FCSTD DOCUMENT  (FreeCAD 0.19R24291 (Git))
Label: Probem 08.pdf
License: All rights reserved
LicenseURL: http://en.wikipedia.org/wiki/All_rights_reserved
objects: Part::Part2DObjectPython×36, App::FeaturePython×35
note: 36 computed .brp shape members not serialized (recipe doc carries the construction recipe); baked Part::Feature solids carry a one-line shape summary decoded from their .brp

FEATURE [Part::Part2DObjectPython] Polygon  # Draft 2D object (typed FeaturePython)
  Area = 0
  ChamferSize = 0
  DrawMode = 0
  FacesNumber = 6
  FilletRadius = 0
  MakeFace = false
  Placement = pos=(-17.9158,-59.1281,0) rot=(0,0,-1;1.5708rad)
  Radius = 25
FEATURE [App::FeaturePython] Text  # WARN: FeaturePython — macro-defined, semantics opaque (R4)
  Placement = pos=(-43.3968,-74.2912,0) rot=(0,0,1;0rad)
  Text = a
FEATURE [App::FeaturePython] Text001  # WARN: FeaturePython — macro-defined, semantics opaque (R4)
  Placement = pos=(-18.9407,-88.9649,0) rot=(0,0,1;0rad)
  Text = b
FEATURE [App::FeaturePython] Text002  # WARN: FeaturePython — macro-defined, semantics opaque (R4)
  Placement = pos=(4.49643,-75.514,0) rot=(0,0,1;0rad)
  Text = c
FEATURE [App::FeaturePython] Text003  # WARN: FeaturePython — macro-defined, semantics opaque (R4)
  Placement = pos=(4.29263,-45.759,0) rot=(0,0,1;0rad)
  Text = d
FEATURE [App::FeaturePython] Text004  # WARN: FeaturePython — macro-defined, semantics opaque (R4)
  Placement = pos=(-16.9027,-31.9005,0) rot=(0,0,1;0rad)
  Text = e
FEATURE [App::FeaturePython] Text005  # WARN: FeaturePython — macro-defined, semantics opaque (R4)
  Placement = pos=(-43.3968,-44.1286,0) rot=(0,0,1;0rad)
  Text = f
FEATURE [App::FeaturePython] Text006  # WARN: FeaturePython — macro-defined, semantics opaque (R4)
  Placement = pos=(-17.9158,-59.1281,0) rot=(0,0,1;0rad)
  Text = O
FEATURE [Part::Part2DObjectPython] Line  # Draft 2D object (typed FeaturePython)
  Area = 0
  ChamferSize = 0
  Closed = false
  End = (-39.5664,-8.08368,0)
  FilletRadius = 0
  Length = 38.5445
  MakeFace = false
  Placement = pos=(-39.5664,-46.6281,0) rot=(0,0,1;0rad)
  Points = (2) [(0,0,0),(0,38.5445,0)]
  Start = (-39.5664,-46.6281,0)
  Subdivisions = 0
FEATURE [Part::Part2DObjectPython] Line002  # Draft 2D object (typed FeaturePython)
  Area = 0
  ChamferSize = 0
  Closed = false
  End = (-17.9158,-8.08368,0)
  FilletRadius = 0
  Length = 26.0445
  MakeFace = false
  Placement = pos=(-17.9158,-34.1281,0) rot=(0,0,1;0rad)
  Points = (2) [(0,0,0),(7.10543e-15,26.0445,0)]
  Start = (-17.9158,-34.1281,0)
  Subdivisions = 0
FEATURE [Part::Part2DObjectPython] Line003  # Draft 2D object (typed FeaturePython)
  Area = 0
  ChamferSize = 0
  Closed = false
  End = (3.73485,-8.08368,0)
  FilletRadius = 0
  Length = 38.5445
  MakeFace = false
  Placement = pos=(3.73485,-46.6281,0) rot=(0,0,1;0rad)
  Points = (2) [(0,0,0),(1.73195e-14,38.5445,0)]
  Start = (3.73485,-46.6281,0)
  Subdivisions = 0
FEATURE [Part::Part2DObjectPython] Line005  # Draft 2D object (typed FeaturePython)
  Area = 0
  ChamferSize = 0
  Closed = false
  End = (-29.4668,15.2405,0)
  FilletRadius = 0
  Length = 25.4169
  MakeFace = false
  Placement = pos=(-39.5664,-8.08368,0) rot=(0,0,1;0rad)
  Points = (2) [(0,0,0),(10.0997,23.3242,0)]
  Start = (-39.5664,-8.08368,0)
  Subdivisions = 0
FEATURE [Part::Part2DObjectPython] Line007  # Draft 2D object (typed FeaturePython)
  Area = 0
  ChamferSize = 0
  Closed = false
  End = (3.73485,-46.6281,0)
  FilletRadius = 0
  Length = 50
  MakeFace = false
  Placement = pos=(-39.5664,-71.6281,0) rot=(0,0,1;0rad)
  Points = (2) [(0,0,0),(43.3013,25,0)]
  Start = (-39.5664,-71.6281,0)
  Subdivisions = 0
FEATURE [Part::Part2DObjectPython] Line008  # Draft 2D object (typed FeaturePython)
  Area = 0
  ChamferSize = 0
  Closed = false
  End = (-39.5664,-46.6281,0)
  FilletRadius = 0
  Length = 50
  MakeFace = false
  Placement = pos=(3.73485,-71.6281,0) rot=(0,0,1;0rad)
  Points = (2) [(0,0,0),(-43.3013,25,0)]
  Start = (3.73485,-71.6281,0)
  Subdivisions = 0
FEATURE [Part::Part2DObjectPython] Line009  # Draft 2D object (typed FeaturePython)
  Area = 0
  ChamferSize = 0
  Closed = false
  End = (-17.9158,-34.1281,0)
  FilletRadius = 0
  Length = 50
  MakeFace = false
  Placement = pos=(-17.9158,-84.1281,0) rot=(0,0,1;0rad)
  Points = (2) [(0,0,0),(2.84217e-14,50,0)]
  Start = (-17.9158,-84.1281,0)
  Subdivisions = 0
FEATURE [Part::Part2DObjectPython] Line010  # Draft 2D object (typed FeaturePython)
  Area = 0
  ChamferSize = 0
  Closed = false
  End = (-17.9158,21.9163,0)
  FilletRadius = 0
  Length = 20
  MakeFace = false
  Placement = pos=(-17.9158,41.9163,0) rot=(0,0,1;0rad)
  Points = (2) [(0,0,0),(0,-20,0)]
  Start = (-17.9158,41.9163,0)
  Subdivisions = 0
FEATURE [Part::Part2DObjectPython] Line012  # Draft 2D object (typed FeaturePython)
  Area = 0
  ChamferSize = 0
  Closed = false
  End = (-69.8239,-8.08368,0)
  FilletRadius = 0
  Length = 88.0582
  MakeFace = false
  Placement = pos=(-17.9158,21.9163,0) rot=(0,0,1;0rad)
  Points = (2) [(24.333,14.0631,0),(-51.9081,-30,0)]
  Start = (6.41717,35.9794,0)
  Subdivisions = 0
FEATURE [App::FeaturePython] Text008  # WARN: FeaturePython — macro-defined, semantics opaque (R4)
  Placement = pos=(-42.9752,-12.9467,0) rot=(0,0,1;0rad)
  Text = a'(f')
FEATURE [App::FeaturePython] Text009  # WARN: FeaturePython — macro-defined, semantics opaque (R4)
  Placement = pos=(-21.1684,-12.9467,0) rot=(0,0,1;0rad)
  Text = b'(e')
FEATURE [App::FeaturePython] Text010  # WARN: FeaturePython — macro-defined, semantics opaque (R4)
  Placement = pos=(-2.82633,-12.9467,0) rot=(0,0,1;0rad)
  Text = c'(d')
FEATURE [App::FeaturePython] Text011  # WARN: FeaturePython — macro-defined, semantics opaque (R4)
  Placement = pos=(-79.6594,-5.81369,0) rot=(0,0,1;0rad)
  Text = VP
FEATURE [App::FeaturePython] Text012  # WARN: FeaturePython — macro-defined, semantics opaque (R4)
  Placement = pos=(-79.4556,-14.5771,0) rot=(0,0,1;0rad)
  Text = HP
FEATURE [App::FeaturePython] Text013  # WARN: FeaturePython — macro-defined, semantics opaque (R4)
  Placement = pos=(-41.5486,16.1968,0) rot=(0,0,1;0rad)
  Text = 1'(6')
FEATURE [App::FeaturePython] Text014  # WARN: FeaturePython — macro-defined, semantics opaque (R4)
  Placement = pos=(-25.6521,21.6995,0) rot=(0,0,1;0rad)
  Text = 2'(5')
FEATURE [App::FeaturePython] Text015  # WARN: FeaturePython — macro-defined, semantics opaque (R4)
  Placement = pos=(-12.7219,28.1305,0) rot=(0,0,1;0rad)
  Text = 3'(4')
FEATURE [Part::Part2DObjectPython] Line015  # Draft 2D object (typed FeaturePython)
  Area = 0
  ChamferSize = 0
  Closed = false
  End = (-17.9158,21.9163,0)
  FilletRadius = 0
  Length = 30
  MakeFace = false
  Placement = pos=(-17.9158,-8.08368,0) rot=(0,0,1;0rad)
  Points = (2) [(0,0,0),(0,30,0)]
  Start = (-17.9158,-8.08368,0)
  Subdivisions = 0
FEATURE [Part::Part2DObjectPython] Arc  # Draft 2D object (typed FeaturePython)
  Area = 0
  FirstAngle = -30
  LastAngle = 0
  MakeFace = false
  Placement = pos=(-17.9158,-59.1281,0) rot=(0,0,1;0rad)
  Radius = 25
FEATURE [Part::Part2DObjectPython] Line017  # Draft 2D object (typed FeaturePython)
  Area = 0
  ChamferSize = 0
  Closed = false
  End = (7.08421,-8.08368,0)
  FilletRadius = 0
  Length = 51.0445
  MakeFace = false
  Placement = pos=(7.08421,-59.1281,0) rot=(0,0,1;0rad)
  Points = (2) [(0,0,0),(-1.77636e-15,51.0445,0)]
  Start = (7.08421,-59.1281,0)
  Subdivisions = 0
FEATURE [Part::Part2DObjectPython] Line018  # Draft 2D object (typed FeaturePython)
  Area = 0
  ChamferSize = 0
  Closed = false
  End = (-10.989,25.9196,0)
  FilletRadius = 0
  Length = 38.508
  MakeFace = false
  Placement = pos=(7.08421,-8.08368,0) rot=(0,0,1;0rad)
  Points = (2) [(0,0,0),(-18.0732,34.0033,0)]
  Start = (7.08421,-8.08368,0)
  Subdivisions = 0
FEATURE [Part::Part2DObjectPython] Line019  # Draft 2D object (typed FeaturePython)
  Area = 0
  ChamferSize = 0
  Closed = false
  End = (-17.9158,41.9163,0)
  FilletRadius = 0
  Length = 29.0693
  MakeFace = false
  Placement = pos=(-39.5664,-8.08368,0) rot=(0,0,1;0rad)
  Points = (2) [(10.0997,23.3242,0),(21.6506,50,0)]
  Start = (-29.4668,15.2405,0)
  Subdivisions = 0
FEATURE [Part::Part2DObjectPython] Line020  # Draft 2D object (typed FeaturePython)
  Area = 0
  ChamferSize = 0
  Closed = false
  End = (-9.25553,21.9163,0)
  FilletRadius = 0
  Length = 0
  MakeFace = false
  Placement = pos=(-9.25553,21.9163,0) rot=(0,0,1;0rad)
  Points = (2) [(0,0,0),(0,3.55271e-15,0)]
  Start = (-9.25553,21.9163,0)
  Subdivisions = 0
FEATURE [Part::Part2DObjectPython] Line021  # Draft 2D object (typed FeaturePython)
  Area = 0
  ChamferSize = 0
  Closed = false
  End = (-9.25553,21.9163,0)
  FilletRadius = 0
  Length = 0
  MakeFace = false
  Placement = pos=(-9.25553,21.9163,0) rot=(0,0,1;0rad)
  Points = (2) [(1.77636e-15,-3.55271e-15,0),(0,0,0)]
  Start = (-9.25553,21.9163,0)
  Subdivisions = 0
FEATURE [App::FeaturePython] Text016  # WARN: FeaturePython — macro-defined, semantics opaque (R4)
  Placement = pos=(-32.0826,-66.0705,0) rot=(0,0,1;0rad)
  Text = 1
FEATURE [App::FeaturePython] Text017  # WARN: FeaturePython — macro-defined, semantics opaque (R4)
  Placement = pos=(-20.5863,-71.1425,0) rot=(0,0,1;0rad)
  Text = 2
FEATURE [App::FeaturePython] Text018  # WARN: FeaturePython — macro-defined, semantics opaque (R4)
  Placement = pos=(-9.59713,-67.5921,0) rot=(0,0,1;0rad)
  Text = 3
FEATURE [App::FeaturePython] Text019  # WARN: FeaturePython — macro-defined, semantics opaque (R4)
  Placement = pos=(-7.06118,-51.7001,0) rot=(0,0,1;0rad)
  Text = 4
FEATURE [App::FeaturePython] Text020  # WARN: FeaturePython — macro-defined, semantics opaque (R4)
  Placement = pos=(-21.0935,-48.4879,0) rot=(0,0,1;0rad)
  Text = 5
FEATURE [App::FeaturePython] Text021  # WARN: FeaturePython — macro-defined, semantics opaque (R4)
  Placement = pos=(-32.928,-55.0814,0) rot=(0,0,1;0rad)
  Text = 6
FEATURE [App::FeaturePython] Text022  # WARN: FeaturePython — macro-defined, semantics opaque (R4)
  Placement = pos=(-7.73743,-58.4626,0) rot=(0,0,1;0rad)
  Text = m
FEATURE [Part::Part2DObjectPython] Line030  # Draft 2D object (typed FeaturePython)
  Area = 0
  ChamferSize = 0
  Closed = false
  End = (-10.989,-53.2967,0)
  FilletRadius = 0
  Length = 0
  MakeFace = false
  Placement = pos=(-17.9158,-50.0736,0) rot=(0,0,1;0rad)
  Points = (2) [(6.92678,-3.22318,0),(6.92678,-3.22318,0)]
  Start = (-10.989,-53.2967,0)
  Subdivisions = 0
FEATURE [Part::Part2DObjectPython] Line031  # Draft 2D object (typed FeaturePython)
  Area = 0
  ChamferSize = 0
  Closed = false
  End = (-10.989,-53.2967,0)
  FilletRadius = 0
  Length = 0
  MakeFace = false
  Placement = pos=(-17.9158,-50.0736,0) rot=(0,0,1;0rad)
  Points = (2) [(6.92678,-3.22318,0),(6.92678,-3.22318,0)]
  Start = (-10.989,-53.2967,0)
  Subdivisions = 0
FEATURE [Part::Part2DObjectPython] Line032  # Draft 2D object (typed FeaturePython)
  Area = 0
  ChamferSize = 0
  Closed = false
  End = (-10.989,-53.2967,0)
  FilletRadius = 0
  Length = 0
  MakeFace = false
  Placement = pos=(-17.9158,-50.0736,0) rot=(0,0,1;0rad)
  Points = (2) [(6.92678,-3.22318,0),(6.92678,-3.22318,0)]
  Start = (-10.989,-53.2967,0)
  Subdivisions = 0
FEATURE [Part::Part2DObjectPython] Line033  # Draft 2D object (typed FeaturePython)
  Area = 0
  ChamferSize = 0
  Closed = false
  End = (-10.989,25.9196,0)
  FilletRadius = 0
  Length = 0
  MakeFace = false
  Placement = pos=(-10.989,25.9196,0) rot=(0,0,1;0rad)
  Points = (2) [(0,0,0),(7.10543e-15,0,0)]
  Start = (-10.989,25.9196,0)
  Subdivisions = 0
FEATURE [Part::Part2DObjectPython] Line034  # Draft 2D object (typed FeaturePython)
  Area = 0
  ChamferSize = 0
  Closed = false
  End = (-10.989,25.9196,0)
  FilletRadius = 0
  Length = 0
  MakeFace = false
  Placement = pos=(-10.989,25.9196,0) rot=(0,0,1;0rad)
  Points = (2) [(0,0,0),(2.84217e-14,0,0)]
  Start = (-10.989,25.9196,0)
  Subdivisions = 0
FEATURE [App::FeaturePython] Dimension  # Draft dimension (typed FeaturePython)
  Diameter = false
  Dimline = (-88.2292,2.44663,0)
  Direction = (0,0,0)
  Distance = 50
  End = (-17.9158,-8.08368,0)
  Normal = (0,0,1)
  Start = (-17.9158,41.9163,0)
FEATURE [App::FeaturePython] Dimension001  # Draft dimension (typed FeaturePython)
  Diameter = false
  Dimline = (-77.4091,26.4537,0)
  Direction = (0,0,0)
  Distance = 20
  End = (-17.9158,21.9163,0)
  Normal = (0,0,1)
  Start = (-17.9158,41.9163,0)
FEATURE [App::FeaturePython] Text023  # WARN: FeaturePython — macro-defined, semantics opaque (R4)
  Placement = pos=(7.79656,-62.8481,0) rot=(0,0,1;0rad)
  Text = q
FEATURE [App::FeaturePython] Text024  # WARN: FeaturePython — macro-defined, semantics opaque (R4)
  Placement = pos=(7.4584,-6.88794,0) rot=(0,0,1;0rad)
  Text = q'
FEATURE [App::FeaturePython] Text025  # WARN: FeaturePython — macro-defined, semantics opaque (R4)
  Placement = pos=(-17.386,41.1595,0) rot=(0,0,1;0rad)
  Text = O'
FEATURE [App::FeaturePython] Dimension002  # Draft dimension (typed FeaturePython)
  Angle = 30.0255
  Center = (-69.8239,-8.08368,0)
  Dimline = (-55.2563,-3.13525,0)
  FirstAngle = 360
  LastAngle = 30.0255
  Normal = (0,0,1)
FEATURE [App::FeaturePython] Dimension003  # Draft dimension (typed FeaturePython)
  Diameter = false
  Dimline = (-75.2112,-63.3803,0)
  Direction = (0,0,0)
  Distance = 25
  End = (-39.5664,-71.6281,0)
  Normal = (0,0,1)
  Start = (-39.5664,-46.6281,0)
FEATURE [Part::Part2DObjectPython] Line036  # Draft 2D object (typed FeaturePython)
  Area = 0
  ChamferSize = 0
  Closed = false
  End = (7.08421,-59.1281,0)
  FilletRadius = 0
  Length = 25
  MakeFace = false
  Placement = pos=(-17.9158,-59.1281,0) rot=(0,0,1;0rad)
  Points = (2) [(0,0,0),(25,-7.10543e-15,0)]
  Start = (-17.9158,-59.1281,0)
  Subdivisions = 0
FEATURE [Part::Part2DObjectPython] Line037  # Draft 2D object (typed FeaturePython)
  Area = 0
  ChamferSize = 0
  Closed = false
  End = (-10.989,25.9196,0)
  FilletRadius = 0
  Length = 21.3418
  MakeFace = false
  Placement = pos=(-29.4668,15.2405,0) rot=(0,0,1;0rad)
  Points = (2) [(0,0,0),(18.4777,10.6791,0)]
  Start = (-29.4668,15.2405,0)
  Subdivisions = 0
FEATURE [Part::Part2DObjectPython] Line038  # Draft 2D object (typed FeaturePython)
  Area = 0
  ChamferSize = 0
  Closed = false
  End = (-10.989,25.9196,0)
  FilletRadius = 0
  Length = 37.0542
  MakeFace = false
  Placement = pos=(3.73485,-8.08368,0) rot=(0,0,1;0rad)
  Points = (2) [(0,0,0),(-14.7239,34.0033,0)]
  Start = (3.73485,-8.08368,0)
  Subdivisions = 0
FEATURE [Part::Part2DObjectPython] Line039  # Draft 2D object (typed FeaturePython)
  Area = 0
  ChamferSize = 0
  Closed = false
  End = (-17.9158,41.9163,0)
  FilletRadius = 0
  Length = 17.432
  MakeFace = false
  Placement = pos=(-10.989,25.9196,0) rot=(0,0,1;0rad)
  Points = (2) [(0,0,0),(-6.92678,15.9967,0)]
  Start = (-10.989,25.9196,0)
  Subdivisions = 0
FEATURE [Part::Part2DObjectPython] Line040  # Draft 2D object (typed FeaturePython)
  Area = 0
  ChamferSize = 0
  Closed = false
  End = (-39.5664,-8.08368,0)
  FilletRadius = 0
  Length = 43.3602
  MakeFace = false
  Placement = pos=(-69.8239,-8.08368,0) rot=(0,0,1;0rad)
  Points = (2) [(-13.1028,-1.77636e-15,0),(30.2575,3.55271e-15,0)]
  Start = (-82.9266,-8.08368,0)
  Subdivisions = 0
FEATURE [Part::Part2DObjectPython] Line041  # Draft 2D object (typed FeaturePython)
  Area = 0
  ChamferSize = 0
  Closed = false
  End = (7.08421,-8.08368,0)
  FilletRadius = 0
  Length = 46.6506
  MakeFace = false
  Placement = pos=(-39.5664,-8.08368,0) rot=(0,0,1;0rad)
  Points = (2) [(0,0,0),(46.6506,-5.32907e-15,0)]
  Start = (-39.5664,-8.08368,0)
  Subdivisions = 0
FEATURE [Part::Part2DObjectPython] Line042  # Draft 2D object (typed FeaturePython)
  Area = 0
  ChamferSize = 0
  Closed = false
  End = (28.674,-8.08368,0)
  FilletRadius = 0
  Length = 21.5897
  MakeFace = false
  Placement = pos=(28.674,-8.08368,0) rot=(0,0,1;0rad)
  Points = (2) [(-21.5897,0,0),(0,0,0)]
  Start = (7.08421,-8.08368,0)
  Subdivisions = 0
FEATURE [Part::Part2DObjectPython] Line043  # Draft 2D object (typed FeaturePython)
  Area = 0
  ChamferSize = 0
  Closed = false
  End = (-29.4668,15.2405,0)
  FilletRadius = 0
  Length = 81.0376
  MakeFace = false
  Placement = pos=(-29.4668,15.2405,0) rot=(0,0,1;0rad)
  Points = (2) [(-7.10543e-15,-81.0376,0),(0,-3.55271e-15,0)]
  Start = (-29.4668,-65.7971,0)
  Subdivisions = 0
FEATURE [Part::Part2DObjectPython] Line044  # Draft 2D object (typed FeaturePython)
  Area = 0
  ChamferSize = 0
  Closed = false
  End = (-10.989,25.9196,0)
  FilletRadius = 0
  Length = 89.0469
  MakeFace = false
  Placement = pos=(-10.989,25.9196,0) rot=(0,0,1;0rad)
  Points = (2) [(3.37508e-14,-89.0469,0),(0,0,0)]
  Start = (-10.989,-63.1273,0)
  Subdivisions = 0
FEATURE [Part::Part2DObjectPython] Wire  # Draft 2D object (typed FeaturePython)
  Area = 272.043
  ChamferSize = 0
  Closed = true
  End = (-29.4668,-52.4592,0)
  FilletRadius = 0
  Length = 62.0765
  MakeFace = true
  Placement = pos=(-29.4668,-65.7971,0) rot=(0,0,1;0rad)
  Points = (6) [(0,0,0),(11.551,-2.38563,0),(18.4777,2.66978,0),(18.4777,10.6681,0),(11.551,15.7235,0),(3.55271e-15,13.3379,0)]
  Start = (-29.4668,-65.7971,0)
  Subdivisions = 0
FEATURE [App::FeaturePython] Text026  # WARN: FeaturePython — macro-defined, semantics opaque (R4)
  Placement = pos=(-84.6953,-7.84313,0) rot=(0,0,1;0rad)
  Text = X
FEATURE [Part::Part2DObjectPython] Line023  # Draft 2D object (typed FeaturePython)
  Area = 0
  ChamferSize = 0
  Closed = false
  End = (-8.8612,21.9163,0)
  FilletRadius = 0
  Length = 81.0445
  MakeFace = false
  Placement = pos=(-8.8612,21.9163,0) rot=(0,0,1;0rad)
  Points = (2) [(2.13163e-14,-81.0445,0),(0,0,0)]
  Start = (-8.8612,-59.1281,0)
  Subdivisions = 0
FEATURE [Part::Part2DObjectPython] Line045  # Draft 2D object (typed FeaturePython)
  Area = 0
  ChamferSize = 0
  Closed = false
  End = (-8.8612,21.9163,0)
  FilletRadius = 0
  Length = 9.05458
  MakeFace = true
  Placement = pos=(-17.9158,21.9163,0) rot=(0,0,1;0rad)
  Points = (2) [(0,0,0),(9.05458,-7.10543e-15,0)]
  Start = (-17.9158,21.9163,0)
  Subdivisions = 0
FEATURE [App::FeaturePython] Text027  # WARN: FeaturePython — macro-defined, semantics opaque (R4)
  Placement = pos=(19.4596,-6.86051,0) rot=(0,0,1;0rad)
  Text = Y
FEATURE [App::FeaturePython] Text028  # WARN: FeaturePython — macro-defined, semantics opaque (R4)
  Placement = pos=(-45.9805,-98.2764,0) rot=(0,0,1;0rad)
  Text = All Dimensions are in mm
FEATURE [App::FeaturePython] Text029  # WARN: FeaturePython — macro-defined, semantics opaque (R4)
  Placement = pos=(-7.94385,21.1568,0) rot=(0,0,1;0rad)
  Text = m'
FEATURE [Part::Part2DObjectPython] Line046  # Draft 2D object (typed FeaturePython)
  Area = 0
  ChamferSize = 0
  Closed = false
  End = (-46.4682,5.41461,0)
  FilletRadius = 0
  Length = 13.1919
  MakeFace = true
  Placement = pos=(-53.0692,16.8362,0) rot=(0,0,1;0rad)
  Points = (2) [(0,0,0),(6.60105,-11.4216,0)]
  Start = (-53.0692,16.8362,0)
  Subdivisions = 0
FEATURE [Part::Part2DObjectPython] Line047  # Draft 2D object (typed FeaturePython)
  Area = 0
  ChamferSize = 0
  Closed = false
  End = (2.85963,33.9234,0)
  FilletRadius = 0
  Length = 11.0372
  MakeFace = true
  Placement = pos=(-2.66323,43.4794,0) rot=(0,0,1;0rad)
  Points = (2) [(0,0,0),(5.52287,-9.55605,0)]
  Start = (-2.66323,43.4794,0)
  Subdivisions = 0
FEATURE [App::FeaturePython] Text030  # WARN: FeaturePython — macro-defined, semantics opaque (R4)
  Placement = pos=(-56.4296,17.0762,0) rot=(0,0,1;0rad)
  Text = S
FEATURE [App::FeaturePython] Text031  # WARN: FeaturePython — macro-defined, semantics opaque (R4)
  Placement = pos=(-6.26366,42.5193,0) rot=(0,0,1;0rad)
  Text = P
